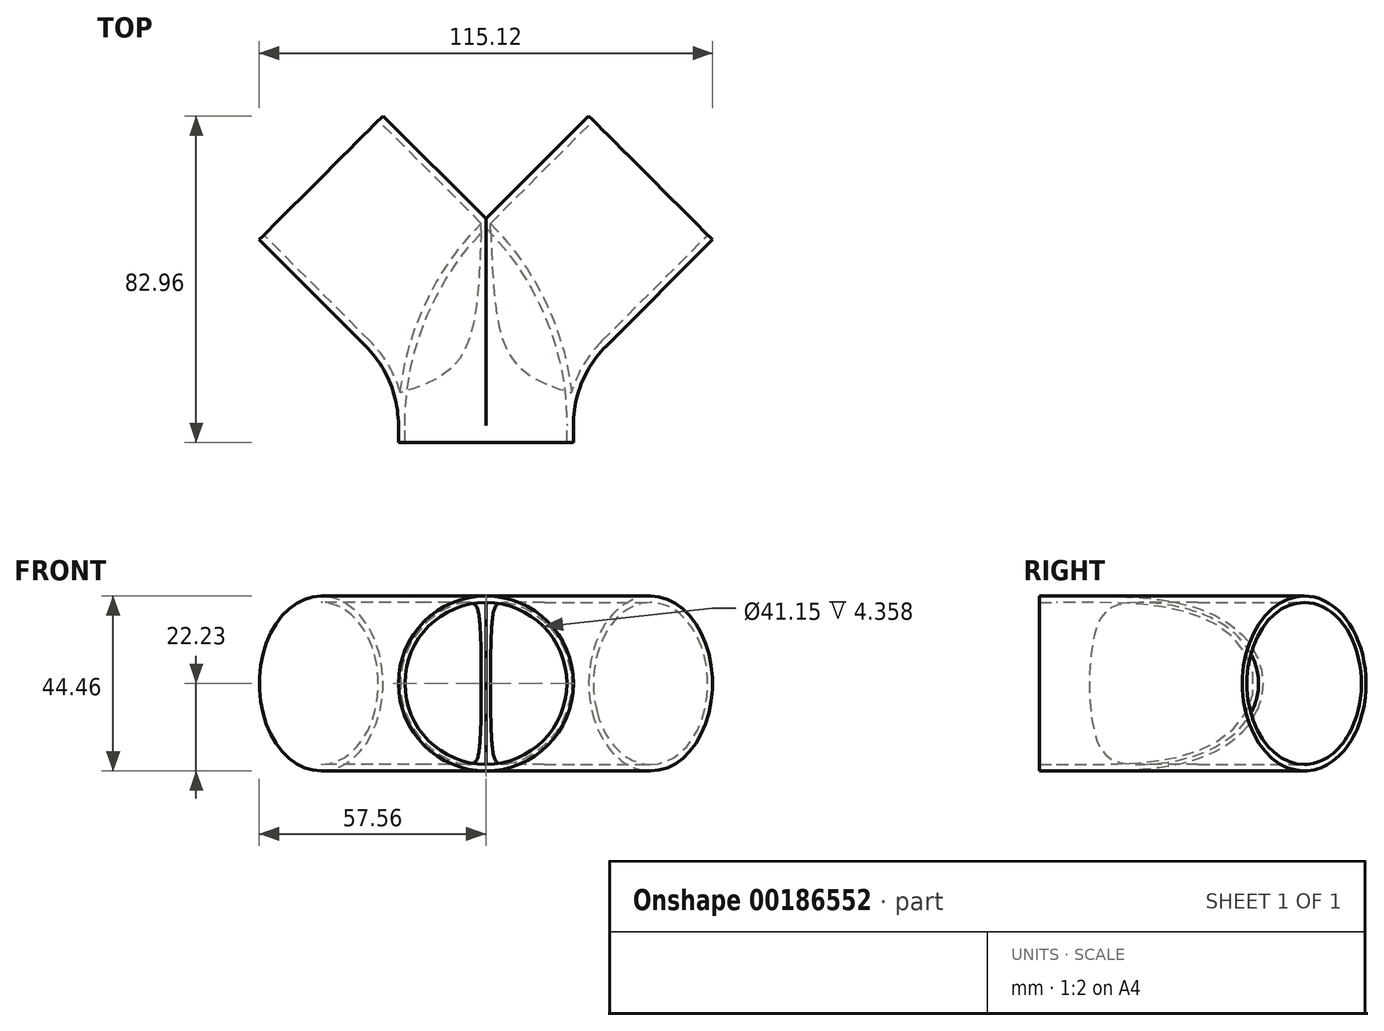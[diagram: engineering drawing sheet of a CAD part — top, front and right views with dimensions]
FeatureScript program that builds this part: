
annotation { "Feature Type Name" : "Feature", "Feature Type Description" : "" }
export const myFeature = defineFeature(function(context is Context, id is Id, definition is map)
    precondition{}
    {
        {
            var Q0;
            Q0=qCreatedBy(makeId("Top.planeOp"),FACE);
            var sketch = newSketch(context, id + "F0", { "sketchPlane" : qUnion([Q0])});
            skLineSegment(sketch, "E0", {"start": v(0, 0) * mm, "end": v(0, 4.36) * mm});
            skLineSegment(sketch, "E1", {"start": v(-14.88, 40.28) * mm, "end": v(-41.85, 67.25) * mm});
            skLineSegment(sketch, "E2", {"start": v(14.88, 40.28) * mm, "end": v(41.85, 67.25) * mm});
            skPoint(sketch, "E3.visualSharp", {"position": v(0, 25.4) * mm});
            skArc(sketch, "E3.filletArc", {"start": v(0, 4.36) * mm, "mid": v(-3.87, 23.8) * mm, "end": v(-14.88, 40.28) * mm});
            skLineSegment(sketch, "E4", {"start": v(0, 4.36) * mm, "end": v(0, 4.36) * mm});
            skArc(sketch, "E5.filletArc", {"start": v(14.88, 40.28) * mm, "mid": v(3.87, 23.8) * mm, "end": v(0, 4.36) * mm});
            skSolve(sketch);
        }
        {
            var Q0;
            Q0=qCreatedBy(makeId("Front.planeOp"),FACE);
            var sketch = newSketch(context, id + "F1", { "sketchPlane" : qUnion([Q0])});
            skCircle(sketch, "E6", {"center": v(0, 0) * mm, "radius": 20.57 * mm});
            skCircle(sketch, "E7", {"center": v(0, 0) * mm, "radius": 22.22 * mm});
            skSolve(sketch);
        }
        {
            var Q0;
            Q0 = qSketchRegion(id + "F1", true);
            var Q1;
            Q1=sQuery(id+"F0.wireOp",EDGE,"E0");
            var Q2;
            Q2=sQuery(id+"F0.wireOp",EDGE,"E5.filletArc");
            var Q3;
            Q3=sQuery(id+"F0.wireOp",EDGE,"E2");
            sweep(context, id + "F2", {"profiles" : qUnion([Q0]), "path" : qUnion([Q1, Q2, Q3])});
        }
        {
            var Q0;
            Q0 = qSketchRegion(id + "F1", true);
            var Q1;
            Q1=sQuery(id+"F0.wireOp",EDGE,"E1");
            var Q2;
            Q2=sQuery(id+"F0.wireOp",EDGE,"E3.filletArc");
            var Q3;
            Q3=sQuery(id+"F0.wireOp",EDGE,"E0");
            sweep(context, id + "F3", {"operationType" : NewBodyOperationType.ADD, "profiles" : qUnion([Q0]), "path" : qUnion([Q1, Q2, Q3])});
        }
    });
